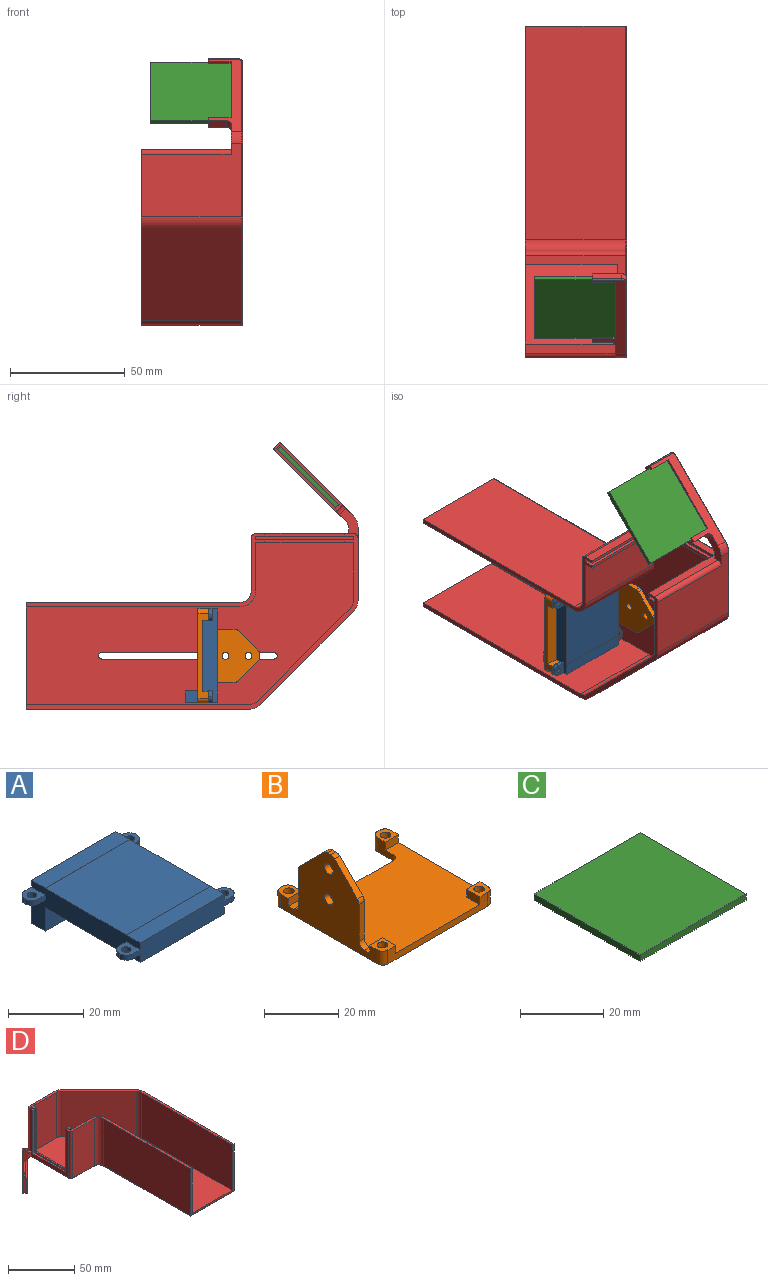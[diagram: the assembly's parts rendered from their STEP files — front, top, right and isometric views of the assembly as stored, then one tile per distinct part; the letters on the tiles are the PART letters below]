
ASSEMBLY  parts=4 mates=7
PART A: 40 faces, bbox 41.9x40.9x14 mm
  f0: plane 5.21x5.08mm, normal (0,0,-1), area 18.6mm2, adj f12,f13,f17,f21,f22,f26,f29
  f1: plane 5.21x5.08mm, normal (0,0,-1), area 18.6mm2, adj f4,f12,f18,f19,f24,f27,f32
  f2: plane 5.21x5.08mm, normal (0,0,-1), area 18.6mm2, adj f8,f14,f16,f20,f21,f25,f30
  f3: plane 31.75x5.21mm, normal (0,0,1), area 165.3mm2, adj f4,f14,f21,f34
  f4: plane 40.89x13.98mm, normal (-1,0,0), area 282.3mm2, adj f1,f3,f5,f10,f11,f12,f14,f23
  f5: plane 5.21x5.08mm, normal (0,0,1), area 18.6mm2, adj f4,f9,f14,f15,f23,f28,f31
  f6: plane 5.21x5.08mm, normal (0,0,1), area 18.6mm2, adj f8,f14,f16,f20,f21,f25,f30
  f7: plane 5.21x5.08mm, normal (0,0,1), area 18.6mm2, adj f12,f13,f17,f21,f22,f26,f29
  f8: plane 1.61x0.13mm, normal (1,0,0), area 0.2mm2, adj f2,f6,f25,f30
  f9: plane 1.61x0.13mm, normal (-1,0,0), area 0.2mm2, adj f5,f11,f28,f31
  f10: plane 5.21x5.08mm, normal (0,0,1), area 18.6mm2, adj f4,f12,f18,f19,f24,f27,f32
  f11: plane 5.21x5.08mm, normal (0,0,-1), area 18.6mm2, adj f4,f9,f14,f15,f23,f28,f31
  f12: plane 36.83x6.36mm, normal (0,-1,0), area 210.2mm2, adj f0,f1,f4,f7,f10,f21,f29,f32
  f13: plane 1.61x0.13mm, normal (1,0,0), area 0.2mm2, adj f0,f7,f26,f29
  f14: plane 36.83x13.98mm, normal (0,1,0), area 452.1mm2, adj f2,f3,f4,f5,f6,f11,f21,f30
  f15: cylinder r=1.27mm len=2.54mm, axis (0,0,-1), area 12.9mm2, adj f5,f11
  f16: cylinder r=1.27mm len=2.54mm, axis (0,0,-1), area 12.9mm2, adj f2,f6
  f17: cylinder r=1.27mm len=2.54mm, axis (0,0,-1), area 12.9mm2, adj f0,f7
  f18: cylinder r=1.27mm len=2.54mm, axis (0,0,-1), area 12.9mm2, adj f1,f10
  f19: plane 1.61x0.13mm, normal (-1,0,0), area 0.2mm2, adj f1,f10,f27,f32
  f20: plane 2.54x1.61mm, normal (0,-1,0), area 4.1mm2, adj f2,f6,f21,f25
  f21: plane 40.89x13.98mm, normal (1,0,0), area 282.3mm2, adj f0,f2,f3,f6,f7,f12,f14,f20
  f22: plane 2.54x1.61mm, normal (0,1,0), area 4.1mm2, adj f0,f7,f21,f26
  f23: plane 2.54x1.61mm, normal (0,-1,0), area 4.1mm2, adj f4,f5,f11,f28
  f24: plane 2.54x1.61mm, normal (0,1,0), area 4.1mm2, adj f1,f4,f10,f27
  f25: cylinder r=2.54mm len=2.54mm, axis (0,0,1), area 6.4mm2, adj f2,f6,f8,f20
  f26: cylinder r=2.54mm len=2.54mm, axis (0,0,-1), area 6.4mm2, adj f0,f7,f13,f22
  f27: cylinder r=2.54mm len=2.54mm, axis (0,0,-1), area 6.4mm2, adj f1,f10,f19,f24
  f28: cylinder r=2.54mm len=2.54mm, axis (0,0,1), area 6.4mm2, adj f5,f9,f11,f23
  f29: cylinder r=2.54mm len=2.54mm, axis (0,0,1), area 6.4mm2, adj f0,f7,f12,f13
  f30: cylinder r=2.54mm len=2.54mm, axis (0,0,-1), area 6.4mm2, adj f2,f6,f8,f14
  f31: cylinder r=2.54mm len=2.54mm, axis (0,0,1), area 6.4mm2, adj f5,f9,f11,f14
  f32: cylinder r=2.54mm len=2.54mm, axis (0,0,-1), area 6.4mm2, adj f1,f10,f12,f19
  f33: plane 31.75x5.21mm, normal (0,0,1), area 165.3mm2, adj f4,f12,f21,f35
  f34: plane 31.75x0.03mm, normal (0,-1,0), area 0.8mm2, adj f3,f4,f21,f36
  f35: plane 31.75x0.03mm, normal (0,1,0), area 0.8mm2, adj f4,f21,f33,f36
  f36: plane 31.75x30.48mm, normal (0,0,1), area 967.7mm2, adj f4,f21,f34,f35
  f37: plane 31.75x7.62mm, normal (0,-1,0), area 241.9mm2, adj f4,f21,f38,f39
  f38: plane 31.75x5.21mm, normal (0,0,-1), area 165.3mm2, adj f4,f14,f21,f37
  f39: plane 35.69x31.75mm, normal (0,0,-1), area 1133.1mm2, adj f4,f12,f21,f37
PART B: 46 faces, bbox 42x41x27 mm
  f0: plane 42x36mm, normal (0,0,1), area 1249.7mm2, adj f2,f3,f5,f7,f8,f10,f11,f13
  f1: plane 4.6x1mm, normal (0,1,0), area 4.6mm2, adj f6,f9,f41,f44
  f2: plane 38x4.6mm, normal (0,-1,0), area 91.6mm2, adj f0,f6,f14,f15,f17,f18,f42,f45
  f3: plane 37x4.6mm, normal (1,0,0), area 89.6mm2, adj f0,f6,f10,f12,f13,f15,f42,f43
  f4: plane 4.6x1mm, normal (0,1,0), area 4.6mm2, adj f6,f12,f40,f43
  f5: plane 37x27mm, normal (-1,0,0), area 548.9mm2, adj f0,f6,f7,f9,f16,f18,f24,f25
  f6: plane 42x41mm, normal (0,0,-1), area 1373.9mm2, adj f1,f2,f3,f4,f5,f8,f11,f19
  f7: plane 5x2.6mm, normal (0,-1,0), area 13mm2, adj f0,f5,f8,f9
  f8: plane 6x4.6mm, normal (1,0,0), area 19.8mm2, adj f0,f6,f7,f9,f38,f41
  f9: plane 5x5mm, normal (0,0,1), area 17.1mm2, adj f1,f5,f7,f8,f22,f41,f44
  f10: plane 5x2.6mm, normal (0,-1,0), area 13mm2, adj f0,f3,f11,f12
  f11: plane 6x4.6mm, normal (-1,0,0), area 19.8mm2, adj f0,f6,f10,f12,f39,f40
  f12: plane 5x5mm, normal (0,0,1), area 17.1mm2, adj f3,f4,f10,f11,f21,f40,f43
  f13: plane 5x2.6mm, normal (0,1,0), area 13mm2, adj f0,f3,f14,f15
  f14: plane 5x2.6mm, normal (-1,0,0), area 13mm2, adj f0,f2,f13,f15
  f15: plane 5x5mm, normal (0,0,1), area 18mm2, adj f2,f3,f13,f14,f20,f42
  f16: plane 5x2.6mm, normal (0,1,0), area 13mm2, adj f0,f5,f17,f18
  f17: plane 5x2.6mm, normal (1,0,0), area 13mm2, adj f0,f2,f16,f18
  f18: plane 5x5mm, normal (0,0,1), area 18mm2, adj f2,f5,f16,f17,f19,f45
  f19: cylinder r=1.4mm len=4.6mm, axis (0,0,1), area 40.5mm2, adj f6,f18
  f20: cylinder r=1.4mm len=4.6mm, axis (0,0,1), area 40.5mm2, adj f6,f15
  f21: cylinder r=1.4mm len=4.6mm, axis (0,0,1), area 40.5mm2, adj f6,f12
  f22: cylinder r=1.4mm len=4.6mm, axis (0,0,1), area 40.5mm2, adj f6,f9
  f23: plane 28x2mm, normal (0,1,0), area 56mm2, adj f0,f6,f38,f39
  f24: plane 12.17x2mm, normal (0,1,0), area 24.3mm2, adj f5,f26,f35,f37
  f25: plane 12.17x2mm, normal (0,-1,0), area 24.3mm2, adj f5,f26,f32,f36
  f26: plane 27x25mm, normal (1,0,0), area 462.2mm2, adj f0,f24,f25,f27,f28,f29,f30,f31
  f27: plane 2x1.34mm, normal (0,0,1), area 2.7mm2, adj f5,f26,f33,f34
  f28: cone r=1.5mm half-angle=4.3deg, axis (-1,0,0), area 19.8mm2, adj f5,f26
  f29: cone r=1.5mm half-angle=4.3deg, axis (-1,0,0), area 19.8mm2, adj f5,f26
  f30: plane 8.83x8.83mm, normal (0,0.71,0.71), area 25mm2, adj f5,f26,f33,f35
  f31: plane 8.83x8.83mm, normal (0,-0.71,0.71), area 25mm2, adj f5,f26,f32,f34
  f32: cylinder r=2mm len=2mm, axis (1,0,0), area 3.1mm2, adj f5,f25,f26,f31
  f33: cylinder r=2mm len=2mm, axis (1,0,0), area 3.1mm2, adj f5,f26,f27,f30
  f34: cylinder r=2mm len=2mm, axis (1,0,0), area 3.1mm2, adj f5,f26,f27,f31
  f35: cylinder r=2mm len=2mm, axis (-1,0,0), area 3.1mm2, adj f5,f24,f26,f30
  f36: cylinder r=2mm len=2mm, axis (1,0,0), area 6.3mm2, adj f0,f5,f25,f26
  f37: cylinder r=2mm len=2mm, axis (-1,0,0), area 6.3mm2, adj f0,f5,f24,f26
  f38: cylinder r=2mm len=2mm, axis (0,0,1), area 6.3mm2, adj f0,f6,f8,f23
  f39: cylinder r=2mm len=2mm, axis (0,0,-1), area 6.3mm2, adj f0,f6,f11,f23
  f40: cylinder r=2mm len=4.6mm, axis (0,0,-1), area 14.5mm2, adj f4,f6,f11,f12
  f41: cylinder r=2mm len=4.6mm, axis (0,0,1), area 14.5mm2, adj f1,f6,f8,f9
  f42: cylinder r=2mm len=4.6mm, axis (0,0,1), area 14.5mm2, adj f2,f3,f6,f15
  f43: cylinder r=2mm len=4.6mm, axis (0,0,-1), area 14.5mm2, adj f3,f4,f6,f12
  f44: cylinder r=2mm len=4.6mm, axis (0,0,1), area 14.5mm2, adj f1,f5,f6,f9
  f45: cylinder r=2mm len=4.6mm, axis (0,0,-1), area 14.5mm2, adj f2,f5,f6,f18
PART C: 6 faces, bbox 36x36x1.9 mm
  f0: plane 36x1.86mm, normal (-1,0,0), area 67mm2, adj f1,f3,f4,f5
  f1: plane 36x1.86mm, normal (0,-1,0), area 67mm2, adj f0,f2,f4,f5
  f2: plane 36x1.86mm, normal (1,0,0), area 67mm2, adj f1,f3,f4,f5
  f3: plane 36x1.86mm, normal (0,1,0), area 67mm2, adj f0,f2,f4,f5
  f4: plane 36x36mm, normal (0,0,1), area 1296mm2, adj f0,f1,f2,f3
  f5: plane 36x36mm, normal (0,0,-1), area 1296mm2, adj f0,f1,f2,f3
PART D: 87 faces, bbox 116.7x145.1x44.2 mm
  f0: plane 143.5x113.92mm, normal (0,0,-1), area 6850.5mm2, adj f57,f58,f59,f60,f61,f65,f66,f67
  f1: plane 12.52x12.52mm, normal (0,0,1), area 29.8mm2, adj f44,f45,f48,f83
  f2: plane 5.01x5.01mm, normal (0,0,1), area 7mm2, adj f44,f45,f82,f83
  f3: plane 31.04x31.04mm, normal (0.71,-0.71,0), area 232.9mm2, adj f5,f7,f8,f10,f11,f12,f42,f49
  f4: plane 25.1x25.1mm, normal (0,0,1), area 34.5mm2, adj f6,f9,f41,f44
  f5: plane 25.1x25.1mm, normal (0,0,1), area 34.5mm2, adj f3,f7,f10,f45
  f6: plane 10x0.71mm, normal (-0.71,-0.71,0), area 10mm2, adj f4,f8,f41,f44
  f7: plane 10x0.71mm, normal (-0.71,-0.71,0), area 10mm2, adj f3,f5,f8,f45
  f8: plane 4.24x4.24mm, normal (0,0,1), area 6mm2, adj f3,f6,f7,f41,f42,f44,f45,f48
  f9: plane 10x0.71mm, normal (0.71,0.71,0), area 10mm2, adj f4,f11,f41,f44
  f10: plane 10x0.71mm, normal (0.71,0.71,0), area 10mm2, adj f3,f5,f11,f45
  f11: plane 4.04x4.04mm, normal (0,0,1), area 5.9mm2, adj f3,f9,f10,f41,f43,f44,f45,f47
  f12: plane 13.05x8.22mm, normal (0,0,1), area 46.9mm2, adj f3,f21,f22,f40,f41,f49,f53,f62
  f13: plane 34.5x1.3mm, normal (0,0,1), area 44.8mm2, adj f16,f17,f32,f36
  f14: plane 104x32mm, normal (0,0,1), area 264.4mm2, adj f17,f20,f21,f23,f24,f28,f29,f32
  f15: plane 144.5x76.5mm, normal (0,0,1), area 395.1mm2, adj f16,f20,f21,f22,f25,f26,f27,f30
  f16: plane 40x1.3mm, normal (0,-1,0), area 52mm2, adj f13,f15,f32,f36
  f17: plane 40x1.3mm, normal (0,1,0), area 52mm2, adj f13,f14,f32,f36
  f18: plane 34.5x1.3mm, normal (0,0,1), area 44.9mm2, adj f21,f33,f34,f38
  f19: plane 142.5x70.5mm, normal (0,0,1), area 6100.9mm2, adj f20,f27,f28,f29,f30,f31,f32,f50
  f20: plane 46.5x43.5mm, normal (0,-1,0), area 237.8mm2, adj f14,f15,f19,f24,f25,f29,f30,f72
  f21: plane 43.5x42.5mm, normal (-1,0,0), area 459.8mm2, adj f12,f14,f15,f18,f33,f34,f40,f68
  f22: plane 43.5x31.86mm, normal (0,1,0), area 1200.3mm2, adj f12,f15,f53,f56,f77,f86
  f23: plane 43.5x23mm, normal (0,-1,0), area 1000.5mm2, adj f14,f52,f69,f84
  f24: plane 93x43.5mm, normal (-1,0,0), area 4045.5mm2, adj f14,f20,f52,f71
  f25: plane 97.1x43.5mm, normal (1,0,0), area 4223.9mm2, adj f15,f20,f55,f73
  f26: plane 43.5x40.4mm, normal (0.71,0.71,0), area 2485.3mm2, adj f15,f55,f56,f75
  f27: plane 42x25.1mm, normal (0,-1,0), area 1054.2mm2, adj f15,f19,f32,f51
  f28: plane 42x21mm, normal (0,1,0), area 882mm2, adj f14,f19,f32,f54
  f29: plane 93x42mm, normal (1,0,0), area 3906mm2, adj f14,f19,f20,f54
  f30: plane 97.1x42mm, normal (-1,0,0), area 4078.2mm2, adj f15,f19,f20,f50
  f31: plane 42x40.4mm, normal (-0.71,-0.71,0), area 2399.6mm2, adj f15,f19,f50,f51
  f32: plane 42.5x42mm, normal (1,0,0), area 405mm2, adj f13,f14,f15,f16,f17,f19,f27,f28
  f33: plane 40x1.3mm, normal (0,-1,0), area 52mm2, adj f15,f18,f21,f38
  f34: plane 40x1.3mm, normal (0,1,0), area 52mm2, adj f14,f18,f21,f38
  f35: plane 42.5x1.4mm, normal (0,0,1), area 59.5mm2, adj f36,f37,f38,f39
  f36: plane 42.5x42mm, normal (-1,0,0), area 405mm2, adj f13,f14,f15,f16,f17,f35,f37,f39
  f37: plane 42x1.4mm, normal (0,-1,0), area 58.8mm2, adj f15,f35,f36,f38
  f38: plane 42.5x42mm, normal (1,0,0), area 405mm2, adj f14,f15,f18,f33,f34,f35,f37,f39
  f39: plane 42x1.4mm, normal (0,1,0), area 58.8mm2, adj f14,f35,f36,f38
  f40: plane 4.5x1.93mm, normal (0,-1,0), area 8.7mm2, adj f12,f21,f49,f67
  f41: plane 31.63x31.63mm, normal (-0.71,0.71,0), area 236.7mm2, adj f4,f6,f8,f9,f11,f12,f42,f53
  f42: plane 8x2.83mm, normal (0.71,0.71,0), area 32mm2, adj f3,f8,f41,f62
  f43: plane 13x2.12mm, normal (-0.71,-0.71,0), area 39mm2, adj f11,f61,f63,f81
  f44: plane 25.81x25.81mm, normal (0.71,-0.71,0), area 56.5mm2, adj f1,f2,f4,f6,f8,f9,f11,f46
  f45: plane 25.81x25.81mm, normal (-0.71,0.71,0), area 56.5mm2, adj f1,f2,f5,f7,f8,f10,f11,f46
  f46: plane 12.52x12.52mm, normal (0,0,1), area 29.8mm2, adj f44,f45,f47,f82
  f47: plane 11x1.41mm, normal (0.71,0.71,0), area 22mm2, adj f11,f44,f45,f46
  f48: plane 11x1.41mm, normal (-0.71,-0.71,0), area 22mm2, adj f1,f8,f44,f45
  f49: cylinder r=5mm len=4.5mm, axis (0,0,1), area 17.7mm2, adj f3,f12,f40,f66
  f50: cylinder r=5mm len=42mm, axis (0,0,1), area 164.9mm2, adj f15,f19,f30,f31
  f51: cylinder r=5mm len=42mm, axis (0,0,1), area 164.9mm2, adj f15,f19,f27,f31
  f52: cylinder r=5mm len=43.5mm, axis (0,0,1), area 341.6mm2, adj f14,f23,f24,f70
  f53: cylinder r=7mm len=4.95mm, axis (0,0,1), area 24.7mm2, adj f12,f22,f41,f78
  f54: cylinder r=7mm len=42mm, axis (0,0,-1), area 461.8mm2, adj f14,f19,f28,f29
  f55: cylinder r=7mm len=43.5mm, axis (0,0,-1), area 239.2mm2, adj f15,f25,f26,f74
  f56: cylinder r=7mm len=43.5mm, axis (0,0,-1), area 239.2mm2, adj f15,f22,f26,f76
  f57: plane 75x2mm, normal (-1,0,0), area 150mm2, adj f0,f19,f58,f60
  f58: cylinder r=1.4mm len=2.8mm, axis (0,0,1), area 8.8mm2, adj f0,f19,f57,f59
  f59: plane 75x2mm, normal (1,0,0), area 150mm2, adj f0,f19,f58,f60
  f60: cylinder r=1.4mm len=2.8mm, axis (0,0,1), area 8.8mm2, adj f0,f19,f57,f59
  f61: cylinder r=2mm len=3.54mm, axis (0.71,-0.71,0), area 9.4mm2, adj f0,f43,f64,f80
  f62: cylinder r=2mm len=4.24mm, axis (0.71,-0.71,0), area 12.6mm2, adj f3,f12,f41,f42
  f63: cylinder r=0.5mm len=13mm, axis (0,0,1), area 10.2mm2, adj f3,f11,f43,f64
  f64: torus R=1.5mm, axis (-0.71,0.71,0), area 2.2mm2, adj f3,f61,f63,f65
  f65: cylinder r=0.5mm len=30.34mm, axis (0.71,0.71,0), area 33.3mm2, adj f0,f3,f64,f66
  f66: torus R=5.5mm, axis (0,0,1), area 3.2mm2, adj f0,f49,f65,f67
  f67: cylinder r=0.5mm len=2.43mm, axis (1,0,0), area 1.7mm2, adj f0,f40,f66,f68
  f68: cylinder r=0.5mm len=41mm, axis (0,-1,0), area 32mm2, adj f0,f21,f67,f85
  f69: cylinder r=0.5mm len=23mm, axis (1,0,0), area 18.1mm2, adj f0,f23,f70,f85
  f70: torus R=5.5mm, axis (0,0,1), area 6.4mm2, adj f0,f52,f69,f71
  f71: cylinder r=0.5mm len=93mm, axis (0,-1,0), area 72.9mm2, adj f0,f24,f70,f72
  f72: cylinder r=0.5mm len=46.5mm, axis (1,0,0), area 36.2mm2, adj f0,f20,f71,f73
  f73: cylinder r=0.5mm len=97.1mm, axis (0,1,0), area 76.1mm2, adj f0,f25,f72,f74
  f74: torus R=6.5mm, axis (0,0,1), area 4.2mm2, adj f0,f55,f73,f75
  f75: cylinder r=0.5mm len=40.75mm, axis (-0.71,0.71,0), area 44.9mm2, adj f0,f26,f74,f76
  f76: torus R=6.5mm, axis (0,0,1), area 4.2mm2, adj f0,f56,f75,f77
  f77: cylinder r=0.5mm len=31.86mm, axis (-1,0,0), area 25mm2, adj f0,f22,f76,f78
  f78: torus R=6.5mm, axis (0,0,1), area 4.2mm2, adj f0,f53,f77,f79
  f79: cylinder r=0.5mm len=30.92mm, axis (-0.71,-0.71,0), area 34mm2, adj f0,f41,f78,f80
  f80: torus R=1.5mm, axis (0.71,-0.71,0), area 2.2mm2, adj f41,f61,f79,f81
  f81: cylinder r=0.5mm len=13mm, axis (0,0,1), area 10.2mm2, adj f11,f41,f43,f80
  f82: cylinder r=1mm len=4mm, axis (0,0,-1), area 25.1mm2, adj f0,f2,f46
  f83: cylinder r=1mm len=4mm, axis (0,0,-1), area 25.1mm2, adj f0,f1,f2
  f84: cylinder r=2mm len=43.5mm, axis (0,0,-1), area 136.7mm2, adj f14,f21,f23,f85
  f85: torus R=1.5mm, axis (0,0,1), area 2.2mm2, adj f0,f68,f69,f84
  f86: cylinder r=2mm len=39mm, axis (0,0,1), area 122.5mm2, adj f12,f15,f21,f22
PLACE A rot(axis=(0,-0.71,0.71),180deg) t=(191.62,-41.35,-121.13)mm
PLACE B rot(axis=(0,-0.71,0.71),180deg) t=(191.62,-36.75,-121.13)mm
PLACE C rot(axis=(0.36,0.36,-0.86),98.4deg) t=(174.62,-71.21,-31.15)mm
PLACE D rot(axis=(0.71,0,-0.71),180deg) t=(214.62,-106.43,-67.88)mm fixed
MATE revolute C.f3 <-> D.f2  axis (1,0,0) through (210.62,-84.59,-43.22)mm
MATE planar B.f5 <-> D.f19  axis (1,0,0) through (212.62,-47.32,-121.13)mm
MATE parallel B.f5 <-> D.f19  axis (1,0,0) through (212.62,-46.84,-109.63)mm
MATE pin_slot B.f29 <-> D.f60  axis (1,0,0) through (212.62,-58.75,-121.13)mm
MATE parallel C.f5 <-> D.f3  axis (0,0.71,-0.71) through (192.62,-83.94,-43.88)mm
MATE parallel D.f27 <-> B.f6  axis (0,1,0) through (191.62,-104.43,-84.43)mm
MATE fastened A.f16 <-> B.f21  axis (0,1,0) through (173.21,-41.35,-138.91)mm
